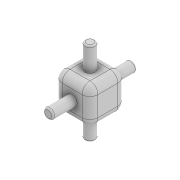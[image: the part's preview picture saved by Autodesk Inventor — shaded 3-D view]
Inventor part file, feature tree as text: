
AUTODESK INVENTOR PART (.ipt)
format: ipt  version: 2020 (Build 240168000, 168)  size: 175,616 bytes
history: native  units: in
note: dims shown in document units (in); Inventor stores cm internally (conversion verified against a paired STEP export)
features: sketch x7, extrude x6, fillet x2, plane x1, revolve x1
ambient origin geometry x8: Origin, YZ Plane, XZ Plane, XY Plane, X Axis, Y Axis, Z Axis, Center Point
bodies: Solid1 (feature_tree)
feature tree (17):
  extrude  "Extrusion1"  Depth=0.1772in
  extrude  "Extrusion2"  Depth=0.1772in
  extrude  "Extrusion3"  Depth=0.1181in TaperAngle=0.0deg
  extrude  "Extrusion4"  Depth=0.1181in TaperAngle=0.0deg
  extrude  "Extrusion5"  Depth=0.0079in
  fillet  "Fillet1"  [1 undecoded]
  fillet  "Fillet2"  Radius=0.0394in
  plane  "Work Plane1"
  revolve  "Revolution1"  [1 undecoded]
  extrude  "Extrusion7"  [1 undecoded]
  sketch  "Sketch1"  dims[d0=0.1772in d1=0.1772in]
  sketch  "Sketch2"  dims[d2=0.1772in d3=0.0in d4=0.0492in]
  sketch  "Sketch3"  dims[d5=0.1181in d6=0.0in d7=0.1181in d8=0.0in]
  sketch  "Sketch4"  dims[d9=0.1181in d10=0.0in d11=0.1181in d12=0.0in]
  sketch  "Sketch5"  dims[d13=0.0394in d14=0.0079in d18=-0.0886in d19=0.0394in]
  sketch  "Sketch8"  dims[d20=90.0deg d21=0.1181in d22=0.0in]
  sketch  "Sketch9"
note: 3 required parameter values undecoded (feature->parameter linkage not recoverable at this tier; creation-order binding heuristic only, values carry confidence <= 0.55)